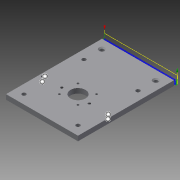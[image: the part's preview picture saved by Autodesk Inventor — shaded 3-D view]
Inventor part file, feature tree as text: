
AUTODESK INVENTOR PART (.ipt)
format: ipt  version: 2015 SP1 (Build 190203100, 203)  size: 367,616 bytes
history: native  units: mm
features: hole x6, pattern_linear x5, extrude x1, sketch x1
ambient origin geometry x8: Origin, YZ Plane, XZ Plane, XY Plane, X Axis, Y Axis, Z Axis, Center Point
bodies: Solid1 (feature_tree)
feature tree (13):
  extrude  "Extrusion1"  Depth=8.0mm TaperAngle=0.0deg
  hole  "Hole1"  [1 undecoded]
  pattern_linear  "Rectangular Pattern1"  Count1=2  [1 undecoded]
  hole  "Hole2"  [1 undecoded]
  pattern_linear  "Rectangular Pattern2"  Spacing1=44.5mm  [1 undecoded]
  hole  "Hole3"  [1 undecoded]
  hole  "Hole4"  [1 undecoded]
  pattern_linear  "Rectangular Pattern3"  Spacing1=0.0mm  [1 undecoded]
  hole  "Hole5"  [1 undecoded]
  hole  "Hole6"  [1 undecoded]
  pattern_linear  "Rectangular Pattern4"  Spacing1=0.0mm  [1 undecoded]
  pattern_linear  "Rectangular Pattern5"  Count1=2 Spacing1=32.0mm
  sketch  "Sketch1"  dims[d1=160.0mm d2=8.0mm d3=0.0mm d4=15.0mm d5=15.0mm d6=6.5mm d7=6.0mm d8=4.0mm d9=2.0mm d10=90.0deg d11=8.0mm d12=20.594885mm d13=20.0mm d15=90.0mm d16=20.0mm d18=100.0mm d19=15.0mm d20=145.0mm d21=6.5mm d22=6.0mm d23=10.0mm d24=2.0mm d25=90.0deg d26=8.0mm d27=20.594885mm d28=20.0mm d30=90.0mm d31=60.0mm d32=60.0mm d33=25.0mm d34=6.0mm d35=4.0mm d36=2.0mm d37=90.0deg d38=8.0mm d39=20.594885mm d40=44.5mm d41=75.5mm d42=3.5mm d43=6.0mm d44=4.0mm d45=2.0mm d46=90.0deg d47=8.0mm d48=20.594885mm d49=20.0mm d51=31.0mm d52=20.0mm d54=31.0mm d55=5.0mm d56=56.0mm d57=4.134mm d58=10.0mm d59=4.0mm d60=2.0mm d61=90.0deg d62=14.2mm d63=20.594885mm d64=0.0mm d65=0.0mm d66=5.0mm d67=56.0mm d68=4.134mm d69=10.0mm d70=4.0mm d71=2.0mm d72=90.0deg d73=14.2mm d74=20.594885mm d75=0.0mm d76=0.0mm d77=20.0mm d79=32.0mm d80=20.0mm d82=32.0mm d83=1.0mm d84=1.0mm]
note: 10 required parameter values undecoded (feature->parameter linkage not recoverable at this tier; creation-order binding heuristic only, values carry confidence <= 0.55)
